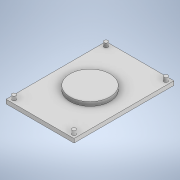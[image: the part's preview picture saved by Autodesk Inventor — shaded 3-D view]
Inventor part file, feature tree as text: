
AUTODESK INVENTOR PART (.ipt)
format: ipt  version: 2022 (Build 260153000, 153)  size: 118,784 bytes
history: native  units: mm
features: extrude x2, sketch x2, other x1
ambient origin geometry x8: Origin, YZ Plane, XZ Plane, XY Plane, X Axis, Y Axis, Z Axis, Center Point
bodies: Body1 (feature_tree)
feature tree (5):
  other  "Твердое тело1"
  extrude  "Выдавливание1"  Depth=25.0mm
  extrude  "Выдавливание2"  Depth=17.0mm
  sketch  "Эскиз1"
  sketch  "Эскиз2"
